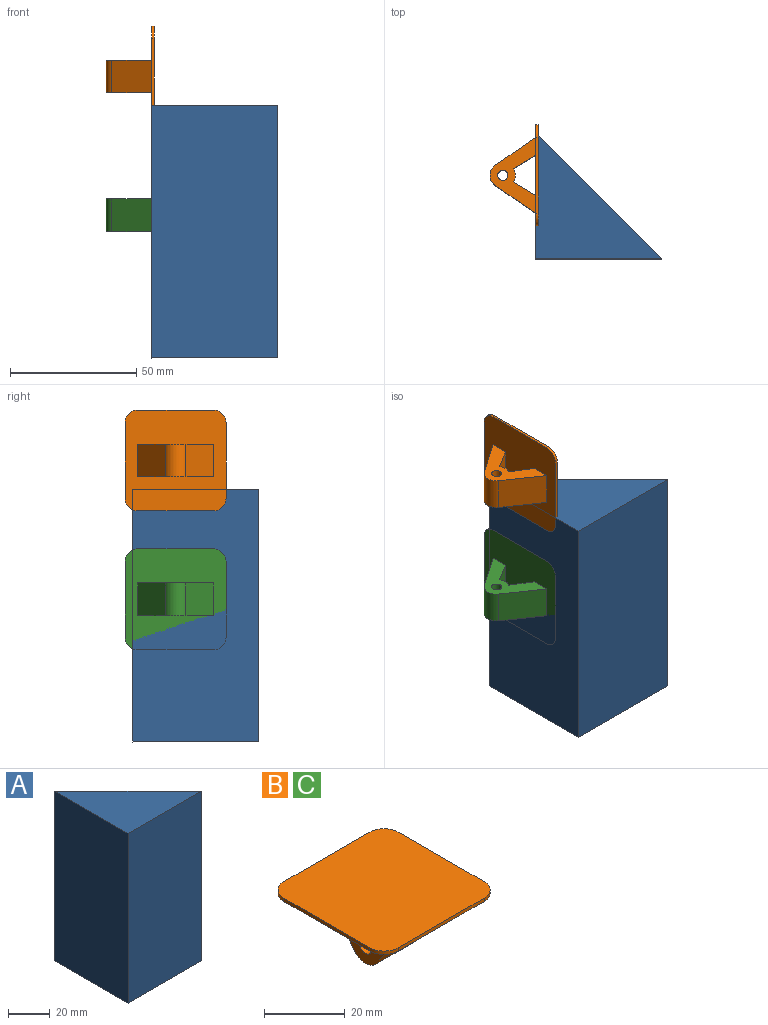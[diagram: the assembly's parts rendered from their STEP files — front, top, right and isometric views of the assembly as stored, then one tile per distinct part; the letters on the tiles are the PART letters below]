
ASSEMBLY  parts=3 mates=1
PART A: 5 faces, bbox 50x50x100 mm
  f0: plane 100x50mm, normal (-1,0,0), area 5000mm2, adj f1,f2,f3,f4
  f1: plane 100x50mm, normal (0,-1,0), area 5000mm2, adj f0,f2,f3,f4
  f2: plane 100x50mm, normal (0.71,0.71,0), area 7071.1mm2, adj f0,f1,f3,f4
  f3: plane 50x50mm, normal (0,0,1), area 1250mm2, adj f0,f1,f2
  f4: plane 50x50mm, normal (0,0,-1), area 1250mm2, adj f0,f1,f2
PART B: 19 faces, bbox 40x40x19 mm
  f0: plane 15.83x13mm, normal (0,-0.82,-0.57), area 249.7mm2, adj f1,f7,f8,f9
  f1: cylinder r=5mm len=13mm, axis (-1,0,0), area 125.9mm2, adj f0,f2,f7,f8
  f2: plane 15.83x13mm, normal (0,0.82,-0.57), area 249.7mm2, adj f1,f7,f8,f9
  f3: plane 13x8.74mm, normal (0,-0.85,0.52), area 133.4mm2, adj f4,f7,f8,f9
  f4: cylinder r=5mm len=13mm, axis (-1,0,0), area 71.7mm2, adj f3,f5,f7,f8
  f5: plane 13x8.74mm, normal (0,0.85,0.52), area 133.4mm2, adj f4,f7,f8,f9
  f6: cylinder r=2mm len=13mm, axis (-1,0,0), area 163.4mm2, adj f7,f8
  f7: plane 30x18mm, normal (1,0,0), area 212.5mm2, adj f0,f1,f2,f3,f4,f5,f6,f9
  f8: plane 30x18mm, normal (-1,0,0), area 212.5mm2, adj f0,f1,f2,f3,f4,f5,f6,f9
  f9: plane 40x40mm, normal (0,0,-1), area 1396.5mm2, adj f0,f2,f3,f5,f7,f8,f10,f11
  f10: plane 30x1mm, normal (1,0,0), area 30mm2, adj f9,f14,f15,f18
  f11: plane 30x1mm, normal (0,1,0), area 30mm2, adj f9,f14,f15,f16
  f12: plane 30x1mm, normal (-1,0,0), area 30mm2, adj f9,f14,f16,f17
  f13: plane 30x1mm, normal (0,-1,0), area 30mm2, adj f9,f14,f17,f18
  f14: plane 40x40mm, normal (0,0,1), area 1578.5mm2, adj f10,f11,f12,f13,f15,f16,f17,f18
  f15: cylinder r=5mm len=5mm, axis (0,0,1), area 7.9mm2, adj f9,f10,f11,f14
  f16: cylinder r=5mm len=5mm, axis (0,0,-1), area 7.9mm2, adj f9,f11,f12,f14
  f17: cylinder r=5mm len=5mm, axis (0,0,1), area 7.9mm2, adj f9,f12,f13,f14
  f18: cylinder r=5mm len=5mm, axis (0,0,-1), area 7.9mm2, adj f9,f10,f13,f14
PART C: same geometry as B
PLACE A rot(axis=(-0.36,-0.91,-0.18),0deg) t=(-5.53,-1.01,15.11)mm
PLACE B rot(axis=(0,1,0),90deg) t=(-32.53,31.99,126.61)mm
PLACE C rot(axis=(0,1,0),90deg) t=(-32.53,31.99,71.61)mm
MATE planar C.f9 <-> A.f0  axis (-1,0,0) through (-5.53,23.99,65.11)mm
